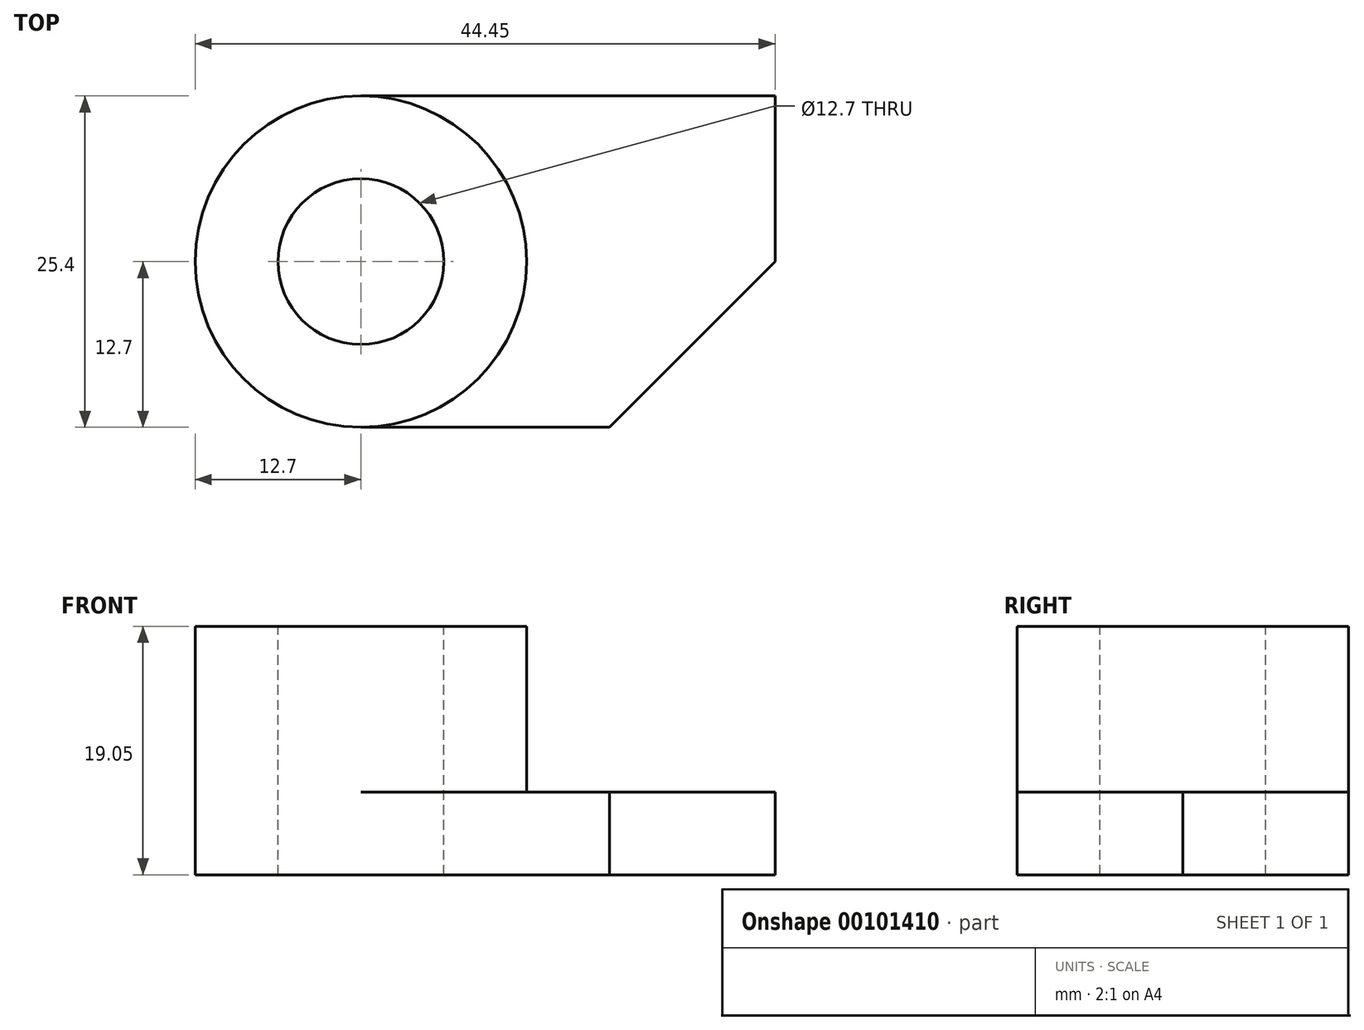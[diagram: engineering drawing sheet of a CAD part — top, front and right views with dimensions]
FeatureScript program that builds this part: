
annotation { "Feature Type Name" : "Feature", "Feature Type Description" : "" }
export const myFeature = defineFeature(function(context is Context, id is Id, definition is map)
    precondition{}
    {
        {
            var Q0;
            Q0=qCreatedBy(makeId("Top.planeOp"),FACE);
            var sketch = newSketch(context, id + "F0", { "sketchPlane" : qUnion([Q0])});
            skLineSegment(sketch, "E0", {"start": v(0, 0) * mm, "end": v(19.05, 0) * mm});
            skLineSegment(sketch, "E1", {"start": v(19.05, 0) * mm, "end": v(31.75, 12.7) * mm});
            skLineSegment(sketch, "E2", {"start": v(31.75, 12.7) * mm, "end": v(31.75, 25.4) * mm});
            skLineSegment(sketch, "E3", {"start": v(31.75, 25.4) * mm, "end": v(0, 25.4) * mm});
            skLineSegment(sketch, "E4", {"start": v(0, 25.4) * mm, "end": v(0, 0) * mm});
            skSolve(sketch);
        }
        {
            var Q0;
            Q0=makeQuery(id+"F0.imprint","IMPRINT",FACE,{"disambiguationData":[TD([[makeQuery(id+"F0.imprint","IMPRINT",EDGE,{"derivedFrom":sQuery(id+"F0.wireOp",EDGE,"E0")}),1.0]])]});
            extrude(context, id + "F1", {"entities" : qUnion([Q0]), "oppositeDirection" : true, "depth" : 6.35 * mm});
        }
        {
            var Q0;
            Q0=makeQuery(id+"F1.opExtrude","CAP_FACE",FACE,{"disambiguationData":[OSD([sQuery(id+"F0.wireOp",EDGE,"E0"),sQuery(id+"F0.wireOp",EDGE,"E1"),sQuery(id+"F0.wireOp",EDGE,"E2"),sQuery(id+"F0.wireOp",EDGE,"E3"),sQuery(id+"F0.wireOp",EDGE,"E4")])],"isStart":true});
            var sketch = newSketch(context, id + "F2", { "sketchPlane" : qUnion([Q0])});
            skCircle(sketch, "E5", {"center": v(0, 12.7) * mm, "radius": 12.7 * mm});
            skSolve(sketch);
        }
        {
            var Q0;
            {var subQ1=makeQuery(id+"F1.opExtrude","CAP_EDGE",EDGE,{"disambiguationData":[OSD([sQuery(id+"F0.wireOp",EDGE,"E4")])],"isStart":true});Q0=makeQuery(id+"F2.imprint","IMPRINT",FACE,{"disambiguationData":[TD([[makeQuery(id+"F2.imprint","IMPRINT",EDGE,{"derivedFrom":subQ1}),-1.0]])]});}
            extrude(context, id + "F3", {"entities" : qUnion([Q0]), "operationType" : NewBodyOperationType.ADD, "oppositeDirection" : true, "depth" : 6.35 * mm});
        }
        {
            var Q0;
            Q0 = qSketchRegion(id + "F2", true);
            extrude(context, id + "F4", {"entities" : qUnion([Q0]), "operationType" : NewBodyOperationType.ADD, "depth" : 12.7 * mm});
        }
        {
            var Q0;
            Q0=makeQuery(id+"F4.opExtrude","CAP_FACE",FACE,{"disambiguationData":[OSD([sQuery(id+"F2.wireOp",EDGE,"E5")])],"isStart":false});
            var sketch = newSketch(context, id + "F5", { "sketchPlane" : qUnion([Q0])});
            skCircle(sketch, "E6", {"center": v(0, 12.7) * mm, "radius": 6.35 * mm});
            skSolve(sketch);
        }
        {
            var Q0;
            Q0 = qSketchRegion(id + "F5", true);
            extrude(context, id + "F6", {"entities" : qUnion([Q0]), "operationType" : NewBodyOperationType.REMOVE, "oppositeDirection" : true, "depth" : 19.05 * mm});
        }
    });
